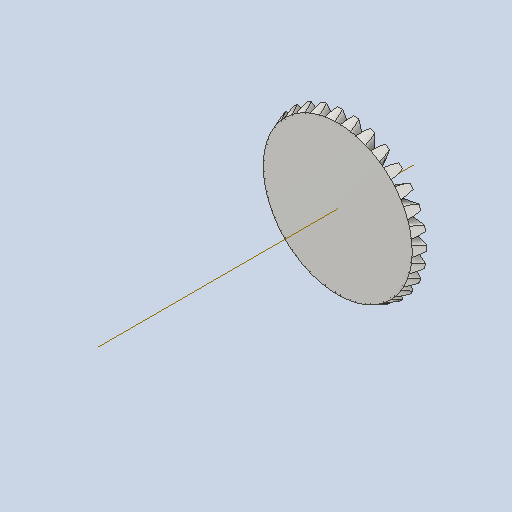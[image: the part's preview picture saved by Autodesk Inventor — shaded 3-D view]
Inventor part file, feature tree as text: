
AUTODESK INVENTOR PART (.ipt)
format: ipt  version: 2022 (Build 260153000, 153)  size: 623,616 bytes
history: native  units: in
note: dims shown in document units (in); Inventor stores cm internally (conversion verified against a paired STEP export)
features: other x30, sketch x1
ambient origin geometry x8: Origin, YZ Plane, XZ Plane, XY Plane, X Axis, Y Axis, Z Axis, Center Point
bodies: Solid1 (feature_tree)
feature tree (31):
  other  "Bevel Gear2"
  other  "Solid1::Bevel Gear2"
  other  "TaggingFeature1"
  other  "Teeth Body Sketch"
  other  "Start Sketch"
  other  "End Sketch"
  other  "End Sketch Right"
  other  "End Sketch Left"
  other  "Body Sketch"
  sketch  "Sketch6"  dims[d0=0.3937in d48=0.0in d49=0.0in d50=90.0deg d52=0.0in d53=0.0in d54=0.0in]
  other  "3D Sketch Right"
  other  "3D Sketch Left"
  other  "Mesh Plane"
  other  "Top Plane"
  other  "Mesh Plane2"
  other  "Tooth Plane"
  other  "End Plane"
  other  "End Plane Right"
  other  "End Plane Left"
  other  "Z Axis_1"
  other  "Top Point"
  other  "Start Point"
  other  "End Point"
  other  "Srf1"
  other  "Srf1::Derived"
  other  "Start plane iMate"
  other  "Mesh iMate2"
  other  "Axis Angle iMate"
  other  "Axis iMate"
  other  "Mesh iMate"
  other  "Intersection iMate"
